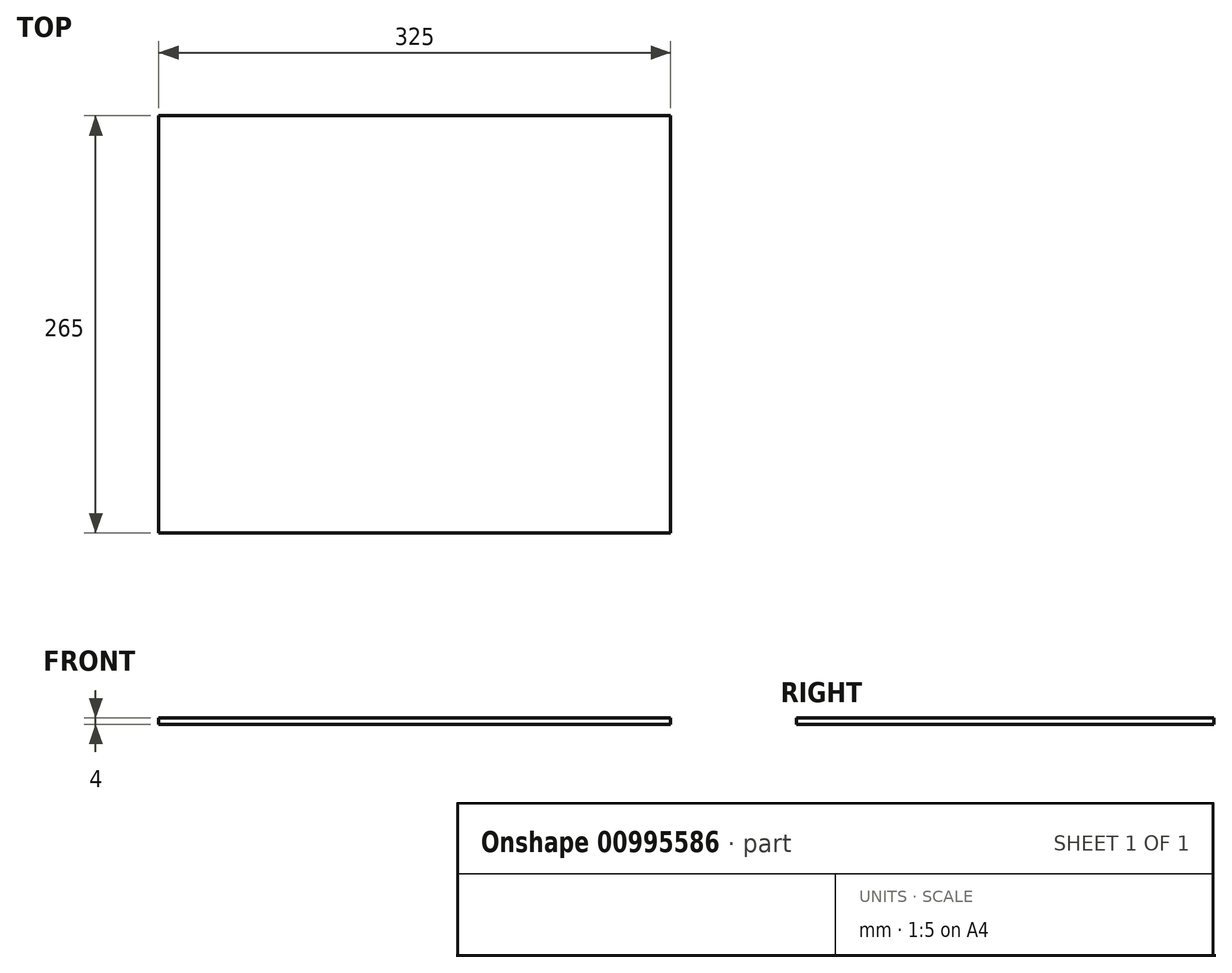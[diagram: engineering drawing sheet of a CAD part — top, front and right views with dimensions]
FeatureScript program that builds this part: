
annotation { "Feature Type Name" : "Feature", "Feature Type Description" : "" }
export const myFeature = defineFeature(function(context is Context, id is Id, definition is map)
    precondition{}
    {
        {
            var Q0;
            Q0=qCreatedBy(makeId("Top.planeOp"),FACE);
            var sketch = newSketch(context, id + "F0", { "sketchPlane" : qUnion([Q0])});
            skLineSegment(sketch, "E0.bottom", {"start": v(0, 0) * mm, "end": v(325, 0) * mm});
            skLineSegment(sketch, "E0.top", {"start": v(0, 265) * mm, "end": v(325, 265) * mm});
            skLineSegment(sketch, "E0.left", {"start": v(0, 0) * mm, "end": v(0, 265) * mm});
            skLineSegment(sketch, "E0.right", {"start": v(325, 0) * mm, "end": v(325, 265) * mm});
            skSolve(sketch);
        }
        {
            var Q0;
            Q0 = qSketchRegion(id + "F0", true);
            extrude(context, id + "F1", {"entities" : qUnion([Q0]), "depth" : 4 * mm, "offsetDistance" : 25 * mm});
        }
    });
